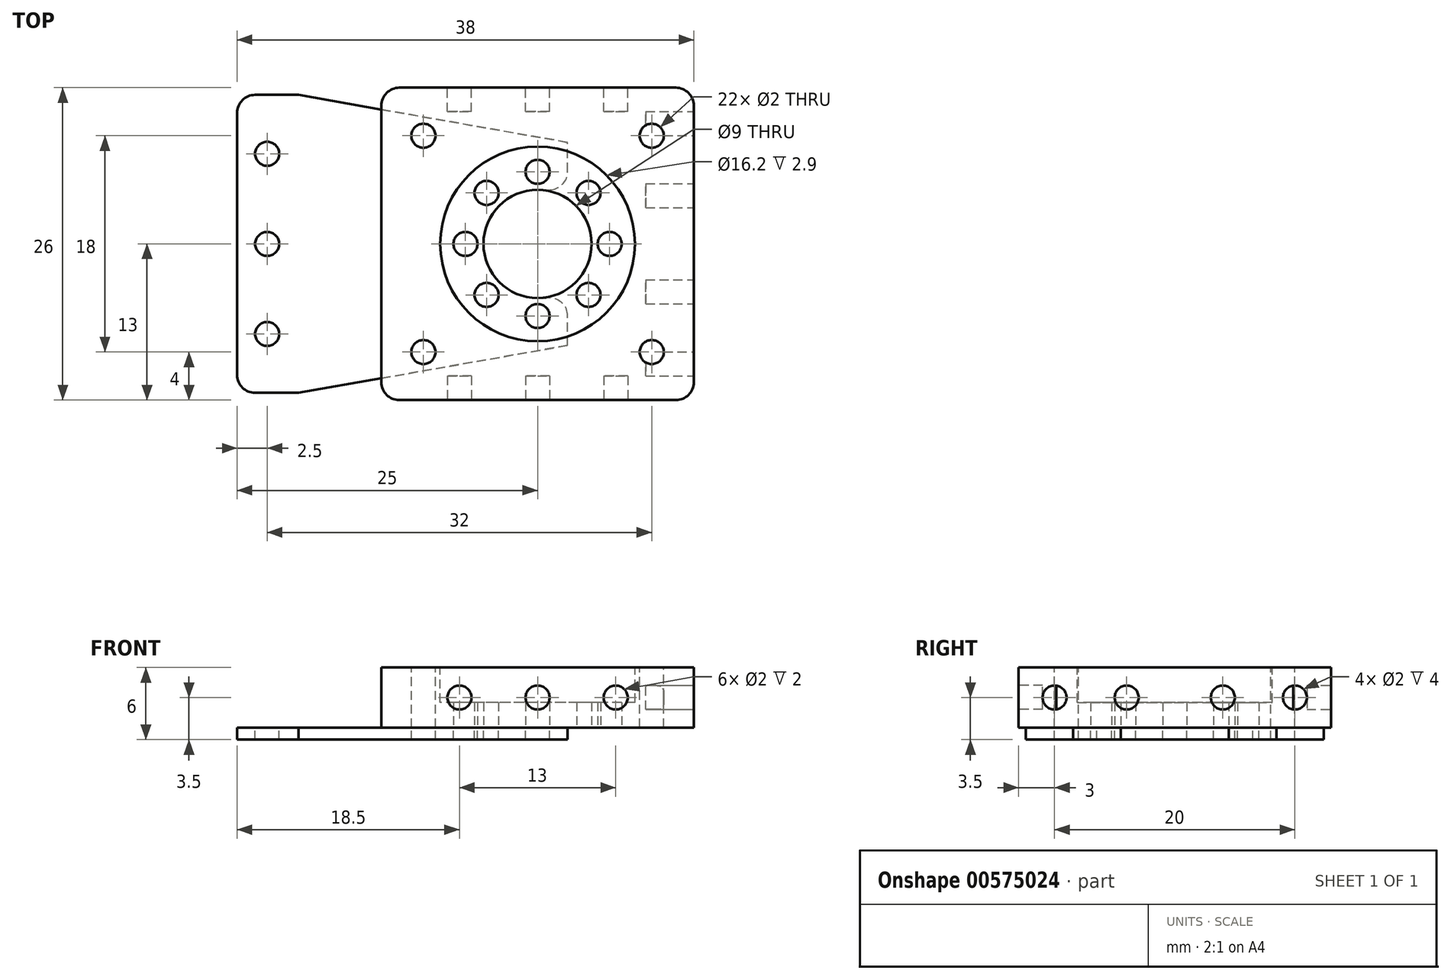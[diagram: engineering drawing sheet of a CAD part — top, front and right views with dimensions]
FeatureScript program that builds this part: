
annotation { "Feature Type Name" : "Feature", "Feature Type Description" : "" }
export const myFeature = defineFeature(function(context is Context, id is Id, definition is map)
    precondition{}
    {
        {
            var Q0;
            Q0=qCreatedBy(makeId("Top.planeOp"),FACE);
            var sketch = newSketch(context, id + "F0", { "sketchPlane" : qUnion([Q0])});
            skLineSegment(sketch, "E0.bottom", {"start": v(-13, 13) * mm, "end": v(13, 13) * mm});
            skLineSegment(sketch, "E0.top", {"start": v(-13, -13) * mm, "end": v(13, -13) * mm});
            skLineSegment(sketch, "E0.left", {"start": v(-13, 13) * mm, "end": v(-13, -13) * mm});
            skLineSegment(sketch, "E0.right", {"start": v(13, 13) * mm, "end": v(13, -13) * mm});
            skPoint(sketch, "E0.middle", {"position": v(0, 0) * mm});
            skCircle(sketch, "E1", {"center": v(0, 0) * mm, "radius": 4.5 * mm});
            skCircle(sketch, "E2", {"center": v(0, 6) * mm, "radius": 1 * mm});
            skCircle(sketch, "E3.1.0", {"center": v(-4.24, 4.24) * mm, "radius": 1 * mm});
            skCircle(sketch, "E3.2.0", {"center": v(-6, 0) * mm, "radius": 1 * mm});
            skCircle(sketch, "E3.3.0", {"center": v(-4.24, -4.24) * mm, "radius": 1 * mm});
            skCircle(sketch, "E3.4.0", {"center": v(0, -6) * mm, "radius": 1 * mm});
            skCircle(sketch, "E3.5.0", {"center": v(4.24, -4.24) * mm, "radius": 1 * mm});
            skCircle(sketch, "E3.6.0", {"center": v(6, 0) * mm, "radius": 1 * mm});
            skCircle(sketch, "E3.7.0", {"center": v(4.24, 4.24) * mm, "radius": 1 * mm});
            skSolve(sketch);
        }
        {
            var Q0;
            Q0=qSketchRegion(id+"F0",true);
            extrude(context, id + "F1", {"entities" : qUnion([Q0]), "depth" : 5 * mm});
        }
        {
            var Q0;
            Q0=makeQuery(id+"F1.opExtrude","SWEPT_FACE",FACE,{"disambiguationData":[OSD([sQuery(id+"F0.wireOp",EDGE,"E0.top")])]});
            var sketch = newSketch(context, id + "F2", { "sketchPlane" : qUnion([Q0])});
            skCircle(sketch, "E4", {"center": v(0, 2.5) * mm, "radius": 1 * mm});
            skPoint(sketch, "E4.centerSnap0", {"position": v(-13, 2.5) * mm});
            skCircle(sketch, "E5", {"center": v(-6.5, 2.5) * mm, "radius": 1 * mm});
            skCircle(sketch, "E6.MirrorC", {"center": v(6.5, 2.5) * mm, "radius": 1 * mm});
            skSolve(sketch);
        }
        {
            var Q0;
            Q0=qSketchRegion(id+"F2",true);
            extrude(context, id + "F3", {"entities" : qUnion([Q0]), "operationType" : NewBodyOperationType.REMOVE, "oppositeDirection" : true, "depth" : 2 * mm});
        }
        {
            var Q0;
            Q0=makeQuery(id+"F1.opExtrude","CAP_FACE",FACE,{"disambiguationData":[OSD([sQuery(id+"F0.wireOp",EDGE,"E0.bottom"),sQuery(id+"F0.wireOp",EDGE,"E0.top"),sQuery(id+"F0.wireOp",EDGE,"E0.left"),sQuery(id+"F0.wireOp",EDGE,"E0.right"),sQuery(id+"F0.wireOp",EDGE,"E1"),sQuery(id+"F0.wireOp",EDGE,"E2"),sQuery(id+"F0.wireOp",EDGE,"E3.1.0"),sQuery(id+"F0.wireOp",EDGE,"E3.2.0"),sQuery(id+"F0.wireOp",EDGE,"E3.3.0"),sQuery(id+"F0.wireOp",EDGE,"E3.4.0"),sQuery(id+"F0.wireOp",EDGE,"E3.5.0"),sQuery(id+"F0.wireOp",EDGE,"E3.6.0"),sQuery(id+"F0.wireOp",EDGE,"E3.7.0")])],"isStart":false});
            var sketch = newSketch(context, id + "F4", { "sketchPlane" : qUnion([Q0])});
            skCircle(sketch, "E7", {"center": v(0, 0) * mm, "radius": 8.1 * mm});
            skSolve(sketch);
        }
        {
            var Q0;
            Q0=qSketchRegion(id+"F4",true);
            extrude(context, id + "F5", {"entities" : qUnion([Q0]), "operationType" : NewBodyOperationType.REMOVE, "oppositeDirection" : true, "depth" : 2.9 * mm});
        }
        {
            var Q0;
            Q0=makeQuery(id+"F1.opExtrude","SWEPT_FACE",FACE,{"disambiguationData":[OSD([sQuery(id+"F0.wireOp",EDGE,"E0.bottom")])]});
            var sketch = newSketch(context, id + "F6", { "sketchPlane" : qUnion([Q0])});
            skCircle(sketch, "E8.0", {"center": v(6.5, 2.5) * mm, "radius": 1 * mm});
            skCircle(sketch, "E9.0", {"center": v(0, 2.5) * mm, "radius": 1 * mm});
            skCircle(sketch, "E10.0", {"center": v(-6.5, 2.5) * mm, "radius": 1 * mm});
            skSolve(sketch);
        }
        {
            var Q0;
            Q0=qSketchRegion(id+"F6",true);
            extrude(context, id + "F7", {"entities" : qUnion([Q0]), "operationType" : NewBodyOperationType.REMOVE, "oppositeDirection" : true, "depth" : 2 * mm});
        }
        {
            var Q0;
            Q0=makeQuery(id+"F1.opExtrude","SWEPT_EDGE",EDGE,{"disambiguationData":[OSD([sQuery(id+"F0.wireOp",EDGE,"E0.top"),sQuery(id+"F0.wireOp",EDGE,"E0.left")])]});
            var Q1;
            Q1=makeQuery(id+"F1.opExtrude","SWEPT_EDGE",EDGE,{"disambiguationData":[OSD([sQuery(id+"F0.wireOp",EDGE,"E0.top"),sQuery(id+"F0.wireOp",EDGE,"E0.right")])]});
            var Q2;
            Q2=makeQuery(id+"F1.opExtrude","SWEPT_EDGE",EDGE,{"disambiguationData":[OSD([sQuery(id+"F0.wireOp",EDGE,"E0.bottom"),sQuery(id+"F0.wireOp",EDGE,"E0.left")])]});
            var Q3;
            Q3=makeQuery(id+"F1.opExtrude","SWEPT_EDGE",EDGE,{"disambiguationData":[OSD([sQuery(id+"F0.wireOp",EDGE,"E0.bottom"),sQuery(id+"F0.wireOp",EDGE,"E0.right")])]});
            fillet(context, id + "F8", {"entities" : qUnion([Q0, Q1, Q2, Q3]), "radius" : 1.5 * mm, "tangentPropagation" : true, "allowEdgeOverflow" : false});
        }
        {
            var Q0;
            Q0=makeQuery(id+"F1.opExtrude","CAP_FACE",FACE,{"disambiguationData":[OSD([sQuery(id+"F0.wireOp",EDGE,"E0.bottom"),sQuery(id+"F0.wireOp",EDGE,"E0.top"),sQuery(id+"F0.wireOp",EDGE,"E0.left"),sQuery(id+"F0.wireOp",EDGE,"E0.right"),sQuery(id+"F0.wireOp",EDGE,"E1"),sQuery(id+"F0.wireOp",EDGE,"E2"),sQuery(id+"F0.wireOp",EDGE,"E3.1.0"),sQuery(id+"F0.wireOp",EDGE,"E3.2.0"),sQuery(id+"F0.wireOp",EDGE,"E3.3.0"),sQuery(id+"F0.wireOp",EDGE,"E3.4.0"),sQuery(id+"F0.wireOp",EDGE,"E3.5.0"),sQuery(id+"F0.wireOp",EDGE,"E3.6.0"),sQuery(id+"F0.wireOp",EDGE,"E3.7.0")])],"isStart":false});
            var sketch = newSketch(context, id + "F9", { "sketchPlane" : qUnion([Q0])});
            skLineSegment(sketch, "E11", {"start": v(-13, 9) * mm, "end": v(13, 9) * mm, "construction": true});
            skCircle(sketch, "E12", {"center": v(-9.5, 9) * mm, "radius": 1 * mm});
            skCircle(sketch, "E13.MirrorC", {"center": v(9.5, 9) * mm, "radius": 1 * mm});
            skCircle(sketch, "E14.MirrorC", {"center": v(-9.5, -9) * mm, "radius": 1 * mm});
            skCircle(sketch, "E15.MirrorC", {"center": v(9.5, -9) * mm, "radius": 1 * mm});
            skSolve(sketch);
        }
        {
            var Q0;
            Q0=qSketchRegion(id+"F9",true);
            extrude(context, id + "F10", {"entities" : qUnion([Q0]), "operationType" : NewBodyOperationType.REMOVE, "endBound" : BoundingType.UP_TO_NEXT, "oppositeDirection" : true, "depth" : 25 * mm});
        }
        {
            var Q0;
            Q0=makeQuery(id+"F1.opExtrude","CAP_FACE",FACE,{"disambiguationData":[OSD([sQuery(id+"F0.wireOp",EDGE,"E0.bottom"),sQuery(id+"F0.wireOp",EDGE,"E0.top"),sQuery(id+"F0.wireOp",EDGE,"E0.left"),sQuery(id+"F0.wireOp",EDGE,"E0.right"),sQuery(id+"F0.wireOp",EDGE,"E1"),sQuery(id+"F0.wireOp",EDGE,"E2"),sQuery(id+"F0.wireOp",EDGE,"E3.1.0"),sQuery(id+"F0.wireOp",EDGE,"E3.2.0"),sQuery(id+"F0.wireOp",EDGE,"E3.3.0"),sQuery(id+"F0.wireOp",EDGE,"E3.4.0"),sQuery(id+"F0.wireOp",EDGE,"E3.5.0"),sQuery(id+"F0.wireOp",EDGE,"E3.6.0"),sQuery(id+"F0.wireOp",EDGE,"E3.7.0")])],"isStart":true});
            var sketch = newSketch(context, id + "F11", { "sketchPlane" : qUnion([Q0])});
            skCircle(sketch, "E16.0", {"center": v(-4.24, -4.24) * mm, "radius": 1 * mm});
            skCircle(sketch, "E17.0", {"center": v(-6, 0) * mm, "radius": 1 * mm});
            skCircle(sketch, "E18.0", {"center": v(-4.24, 4.24) * mm, "radius": 1 * mm});
            skCircle(sketch, "E19.0", {"center": v(0, 6) * mm, "radius": 1 * mm});
            skCircle(sketch, "E20.0", {"center": v(0, -6) * mm, "radius": 1 * mm});
            skArc(sketch, "E21.0", {"start": v(0, 4.5) * mm, "mid": v(-4.5, 0) * mm, "end": v(0, -4.5) * mm});
            skLineSegment(sketch, "E22.bottom", {"start": v(2.5, 12.4) * mm, "end": v(-25, 12.4) * mm});
            skLineSegment(sketch, "E22.top", {"start": v(2.5, -12.4) * mm, "end": v(-25, -12.4) * mm});
            skLineSegment(sketch, "E22.left", {"start": v(2.5, 12.4) * mm, "end": v(2.5, -12.4) * mm});
            skLineSegment(sketch, "E22.right", {"start": v(-25, 12.4) * mm, "end": v(-25, -12.4) * mm});
            skPoint(sketch, "E22.middle", {"position": v(-11.25, 0) * mm});
            skLineSegment(sketch, "E23", {"start": v(0, 4.5) * mm, "end": v(2.5, 4.5) * mm});
            skLineSegment(sketch, "E24.MirrorCS", {"start": v(0, -4.5) * mm, "end": v(2.5, -4.5) * mm});
            skCircle(sketch, "E25", {"center": v(-22.5, 0) * mm, "radius": 1 * mm});
            skCircle(sketch, "E26", {"center": v(-22.5, 7.5) * mm, "radius": 1 * mm});
            skCircle(sketch, "E27.MirrorC", {"center": v(-22.5, -7.5) * mm, "radius": 1 * mm});
            skSolve(sketch);
        }
        {
            var Q0;
            Q0=makeQuery(id+"F11.imprint","IMPRINT",FACE,{"disambiguationData":[TD([[makeQuery(id+"F11.imprint","IMPRINT",EDGE,{"derivedFrom":makeQuery(id+"F10.boolean.opBoolean","COPY",EDGE,{"derivedFrom":makeQuery(id+"F10.opExtrude","TWEAK_EDGE",EDGE,{"derivedFrom":[makeQuery(id+"F1.opExtrude","CAP_FACE",FACE,{"disambiguationData":[OSD([sQuery(id+"F0.wireOp",EDGE,"E0.bottom"),sQuery(id+"F0.wireOp",EDGE,"E0.top"),sQuery(id+"F0.wireOp",EDGE,"E0.left"),sQuery(id+"F0.wireOp",EDGE,"E0.right"),sQuery(id+"F0.wireOp",EDGE,"E1"),sQuery(id+"F0.wireOp",EDGE,"E2"),sQuery(id+"F0.wireOp",EDGE,"E3.1.0"),sQuery(id+"F0.wireOp",EDGE,"E3.2.0"),sQuery(id+"F0.wireOp",EDGE,"E3.3.0"),sQuery(id+"F0.wireOp",EDGE,"E3.4.0"),sQuery(id+"F0.wireOp",EDGE,"E3.5.0"),sQuery(id+"F0.wireOp",EDGE,"E3.6.0"),sQuery(id+"F0.wireOp",EDGE,"E3.7.0")])],"isStart":true}),makeQuery(id+"F9.imprint","IMPRINT",EDGE,{"derivedFrom":sQuery(id+"F9.wireOp",EDGE,"E12")})]})})}),1.0]])]});
            var Q1;
            Q1=makeQuery(id+"F11.imprint","IMPRINT",FACE,{"disambiguationData":[TD([[makeQuery(id+"F11.imprint","IMPRINT",EDGE,{"derivedFrom":makeQuery(id+"F10.boolean.opBoolean","COPY",EDGE,{"derivedFrom":makeQuery(id+"F10.opExtrude","TWEAK_EDGE",EDGE,{"derivedFrom":[makeQuery(id+"F1.opExtrude","CAP_FACE",FACE,{"disambiguationData":[OSD([sQuery(id+"F0.wireOp",EDGE,"E0.bottom"),sQuery(id+"F0.wireOp",EDGE,"E0.top"),sQuery(id+"F0.wireOp",EDGE,"E0.left"),sQuery(id+"F0.wireOp",EDGE,"E0.right"),sQuery(id+"F0.wireOp",EDGE,"E1"),sQuery(id+"F0.wireOp",EDGE,"E2"),sQuery(id+"F0.wireOp",EDGE,"E3.1.0"),sQuery(id+"F0.wireOp",EDGE,"E3.2.0"),sQuery(id+"F0.wireOp",EDGE,"E3.3.0"),sQuery(id+"F0.wireOp",EDGE,"E3.4.0"),sQuery(id+"F0.wireOp",EDGE,"E3.5.0"),sQuery(id+"F0.wireOp",EDGE,"E3.6.0"),sQuery(id+"F0.wireOp",EDGE,"E3.7.0")])],"isStart":true}),makeQuery(id+"F9.imprint","IMPRINT",EDGE,{"derivedFrom":sQuery(id+"F9.wireOp",EDGE,"E14.MirrorC")})]})})}),-1.0]])]});
            var Q2;
            {var subQ17=sQuery(id+"F11.wireOp",EDGE,"E22.right");Q2=makeQuery(id+"F11.imprint","IMPRINT",FACE,{"disambiguationData":[TD([[makeQuery(id+"F11.imprint","IMPRINT",EDGE,{"derivedFrom":subQ17}),1.0]])]});}
            var Q3;
            Q3=makeQuery(id+"F11.imprint","IMPRINT",FACE,{"disambiguationData":[TD([[makeQuery(id+"F11.imprint","IMPRINT",EDGE,{"derivedFrom":sQuery(id+"F11.wireOp",EDGE,"E16.0")}),1.0]])]});
            extrude(context, id + "F12", {"entities" : qUnion([Q0, Q1, Q2, Q3]), "offsetDistance" : 25 * mm, "depth" : 1 * mm});
        }
        {
            var Q0;
            Q0=makeQuery(id+"F12.opExtrude","CAP_FACE",FACE,{"disambiguationData":[OSD([sQuery(id+"F11.wireOp",EDGE,"E16.0"),sQuery(id+"F11.wireOp",EDGE,"E17.0"),sQuery(id+"F11.wireOp",EDGE,"E18.0"),sQuery(id+"F11.wireOp",EDGE,"E19.0"),sQuery(id+"F11.wireOp",EDGE,"E20.0"),sQuery(id+"F11.wireOp",EDGE,"E21.0"),sQuery(id+"F11.wireOp",EDGE,"E22.bottom"),sQuery(id+"F11.wireOp",EDGE,"E22.top"),sQuery(id+"F11.wireOp",EDGE,"E22.left"),sQuery(id+"F11.wireOp",EDGE,"E22.right"),sQuery(id+"F11.wireOp",EDGE,"E23"),sQuery(id+"F11.wireOp",EDGE,"E24.MirrorCS"),sQuery(id+"F11.wireOp",EDGE,"E25"),sQuery(id+"F11.wireOp",EDGE,"E26"),sQuery(id+"F11.wireOp",EDGE,"E27.MirrorC")])],"isStart":false});
            var sketch = newSketch(context, id + "F13", { "sketchPlane" : qUnion([Q0])});
            skLineSegment(sketch, "E28", {"start": v(2.5, 8.45) * mm, "end": v(-19.9, 12.4) * mm});
            skLineSegment(sketch, "E29", {"start": v(-19.9, 12.4) * mm, "end": v(2.5, 12.4) * mm});
            skLineSegment(sketch, "E30", {"start": v(2.5, 12.4) * mm, "end": v(2.5, 8.45) * mm});
            skLineSegment(sketch, "E31.MirrorCS", {"start": v(2.5, -12.4) * mm, "end": v(2.5, -8.45) * mm});
            skLineSegment(sketch, "E32.MirrorCS", {"start": v(2.5, -8.45) * mm, "end": v(-19.9, -12.4) * mm});
            skLineSegment(sketch, "E33.MirrorCS", {"start": v(-19.9, -12.4) * mm, "end": v(2.5, -12.4) * mm});
            skSolve(sketch);
        }
        {
            var Q0;
            Q0=qSketchRegion(id+"F13",true);
            extrude(context, id + "F14", {"entities" : qUnion([Q0]), "operationType" : NewBodyOperationType.REMOVE, "endBound" : BoundingType.UP_TO_NEXT, "oppositeDirection" : true, "depth" : 25 * mm});
        }
        {
            var Q0;
            Q0=makeQuery(id+"F14.boolean.opBoolean","COPY",EDGE,{"derivedFrom":makeQuery(id+"F14.opExtrude","SWEPT_EDGE",EDGE,{"disambiguationData":[OSD([sQuery(id+"F11.wireOp",EDGE,"E22.left"),sQuery(id+"F13.wireOp",EDGE,"E28"),sQuery(id+"F13.wireOp",EDGE,"E30")])]})});
            var Q1;
            Q1=makeQuery(id+"F14.boolean.opBoolean","COPY",EDGE,{"derivedFrom":makeQuery(id+"F14.opExtrude","SWEPT_EDGE",EDGE,{"disambiguationData":[OSD([sQuery(id+"F11.wireOp",EDGE,"E22.bottom"),sQuery(id+"F13.wireOp",EDGE,"E28"),sQuery(id+"F13.wireOp",EDGE,"E29")])]})});
            var Q2;
            Q2=makeQuery(id+"F12.opExtrude","SWEPT_EDGE",EDGE,{"disambiguationData":[OSD([sQuery(id+"F11.wireOp",EDGE,"E22.bottom"),sQuery(id+"F11.wireOp",EDGE,"E22.right")])]});
            var Q3;
            Q3=makeQuery(id+"F12.opExtrude","SWEPT_EDGE",EDGE,{"disambiguationData":[OSD([sQuery(id+"F11.wireOp",EDGE,"E22.left"),sQuery(id+"F11.wireOp",EDGE,"E24.MirrorCS")])]});
            var Q4;
            Q4=makeQuery(id+"F12.opExtrude","SWEPT_EDGE",EDGE,{"disambiguationData":[OSD([sQuery(id+"F11.wireOp",EDGE,"E22.left"),sQuery(id+"F11.wireOp",EDGE,"E23")])]});
            var Q5;
            Q5=makeQuery(id+"F14.boolean.opBoolean","COPY",EDGE,{"derivedFrom":makeQuery(id+"F14.opExtrude","SWEPT_EDGE",EDGE,{"disambiguationData":[OSD([sQuery(id+"F11.wireOp",EDGE,"E22.left"),sQuery(id+"F13.wireOp",EDGE,"E31.MirrorCS"),sQuery(id+"F13.wireOp",EDGE,"E32.MirrorCS")])]})});
            var Q6;
            Q6=makeQuery(id+"F14.boolean.opBoolean","COPY",EDGE,{"derivedFrom":makeQuery(id+"F14.opExtrude","SWEPT_EDGE",EDGE,{"disambiguationData":[OSD([sQuery(id+"F11.wireOp",EDGE,"E22.top"),sQuery(id+"F13.wireOp",EDGE,"E32.MirrorCS"),sQuery(id+"F13.wireOp",EDGE,"E33.MirrorCS")])]})});
            var Q7;
            Q7=makeQuery(id+"F12.opExtrude","SWEPT_EDGE",EDGE,{"disambiguationData":[OSD([sQuery(id+"F11.wireOp",EDGE,"E22.top"),sQuery(id+"F11.wireOp",EDGE,"E22.right")])]});
            fillet(context, id + "F15", {"entities" : qUnion([Q0, Q1, Q2, Q3, Q4, Q5, Q6, Q7]), "radius" : 1.5 * mm, "tangentPropagation" : true, "allowEdgeOverflow" : false});
        }
        {
            var Q0;
            Q0=makeQuery(id+"F1.opExtrude","SWEPT_FACE",FACE,{"disambiguationData":[OSD([sQuery(id+"F0.wireOp",EDGE,"E0.right")])]});
            var sketch = newSketch(context, id + "F16", { "sketchPlane" : qUnion([Q0])});
            skPoint(sketch, "E34.0", {"position": v(-13, 2.5) * mm});
            skPoint(sketch, "E35.0", {"position": v(13, 2.5) * mm});
            skLineSegment(sketch, "E36", {"start": v(-13, 2.5) * mm, "end": v(13, 2.5) * mm, "construction": true});
            skCircle(sketch, "E37", {"center": v(-4, 2.5) * mm, "radius": 1 * mm});
            skCircle(sketch, "E38", {"center": v(-10, 2.5) * mm, "radius": 1 * mm});
            skCircle(sketch, "E39.MirrorC", {"center": v(4, 2.5) * mm, "radius": 1 * mm});
            skCircle(sketch, "E40.MirrorC", {"center": v(10, 2.5) * mm, "radius": 1 * mm});
            skSolve(sketch);
        }
        {
            var Q0;
            Q0=qSketchRegion(id+"F16",true);
            extrude(context, id + "F17", {"entities" : qUnion([Q0]), "operationType" : NewBodyOperationType.REMOVE, "oppositeDirection" : true, "depth" : 4 * mm, "offsetDistance" : 25 * mm});
        }
    });
